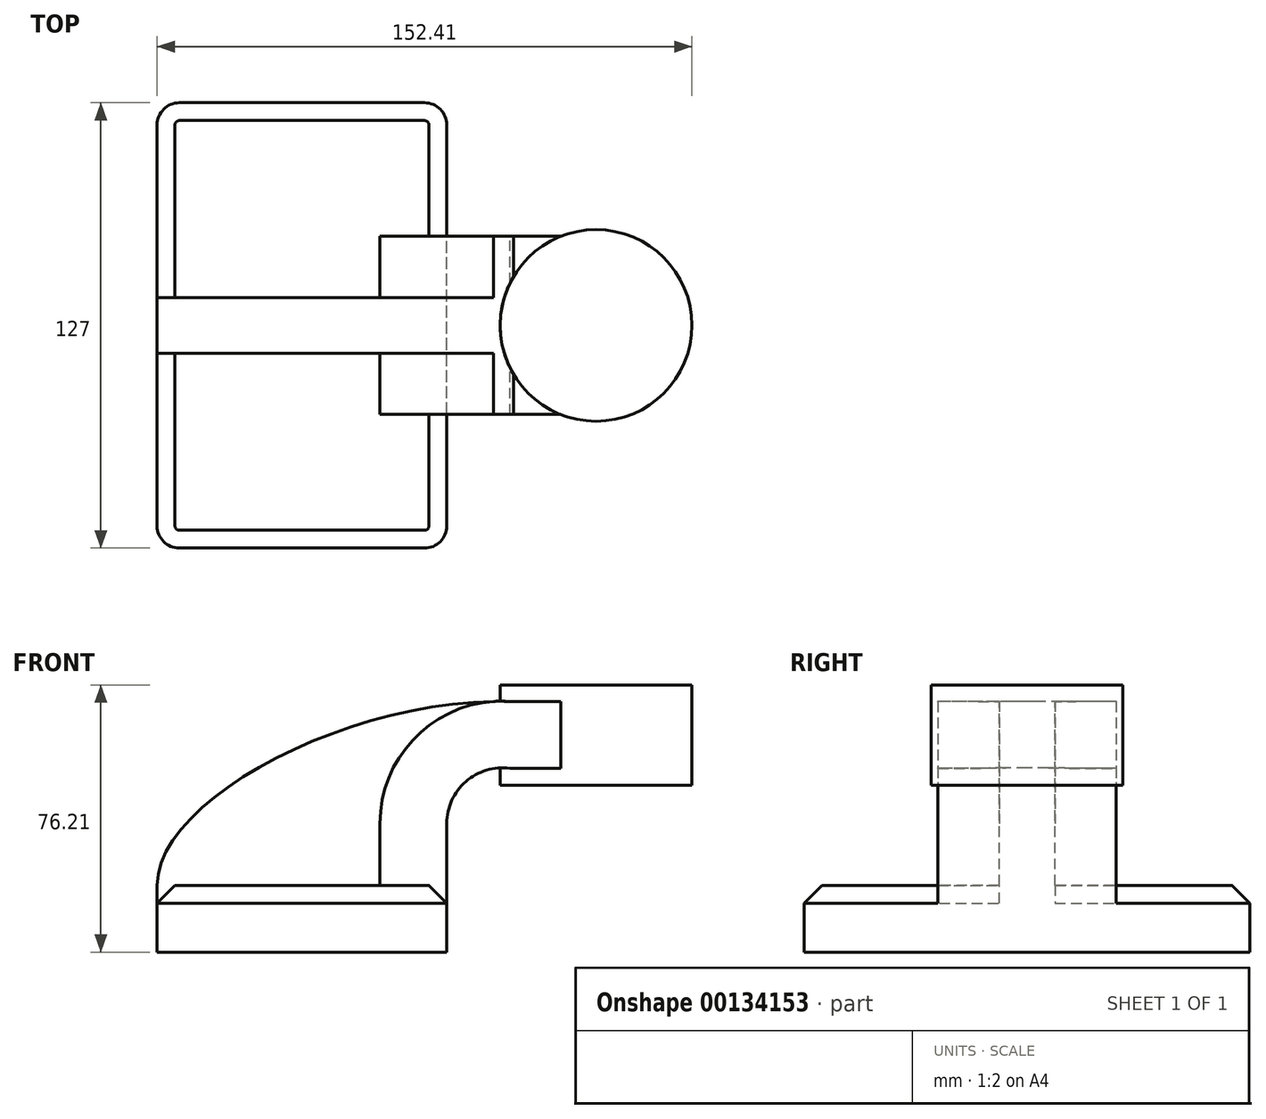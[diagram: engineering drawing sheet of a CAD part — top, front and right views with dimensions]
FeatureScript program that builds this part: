
annotation { "Feature Type Name" : "Feature", "Feature Type Description" : "" }
export const myFeature = defineFeature(function(context is Context, id is Id, definition is map)
    precondition{}
    {
        {
            var Q0;
            Q0=qCreatedBy(makeId("Front.planeOp"),FACE);
            var sketch = newSketch(context, id + "F0", { "sketchPlane" : qUnion([Q0])});
            skLineSegment(sketch, "E0.bottom", {"start": v(41.27, 9.53) * mm, "end": v(-41.28, 9.53) * mm});
            skLineSegment(sketch, "E0.top", {"start": v(41.28, -9.52) * mm, "end": v(-41.28, -9.52) * mm});
            skLineSegment(sketch, "E0.left", {"start": v(41.28, 9.53) * mm, "end": v(41.28, -9.52) * mm});
            skLineSegment(sketch, "E0.right", {"start": v(-41.28, 9.53) * mm, "end": v(-41.27, -9.52) * mm});
            skPoint(sketch, "E0.middle", {"position": v(0, 0) * mm});
            skLineSegment(sketch, "E1.bottom", {"start": v(111.12, 66.68) * mm, "end": v(60.32, 66.68) * mm});
            skLineSegment(sketch, "E1.top", {"start": v(111.12, 38.1) * mm, "end": v(60.32, 38.1) * mm});
            skLineSegment(sketch, "E1.left", {"start": v(111.12, 66.68) * mm, "end": v(111.12, 38.1) * mm});
            skLineSegment(sketch, "E1.right", {"start": v(60.32, 66.68) * mm, "end": v(60.32, 38.1) * mm});
            skPoint(sketch, "E1.middle", {"position": v(85.72, 52.39) * mm});
            skLineSegment(sketch, "E2", {"start": v(41.27, 9.53) * mm, "end": v(41.27, 27.14) * mm});
            skArc(sketch, "E3", {"start": v(41.27, 27.14) * mm, "mid": v(46.7, 39.09) * mm, "end": v(59.26, 42.88) * mm});
            skLineSegment(sketch, "E4", {"start": v(59.26, 42.88) * mm, "end": v(83.8, 42.88) * mm});
            skLineSegment(sketch, "E5.0", {"start": v(60.28, 61.93) * mm, "end": v(83.8, 61.93) * mm});
            skArc(sketch, "E5.1", {"start": v(22.22, 27.14) * mm, "mid": v(33.59, 52.92) * mm, "end": v(60.28, 61.93) * mm});
            skLineSegment(sketch, "E5.2", {"start": v(22.22, 9.53) * mm, "end": v(22.22, 27.14) * mm});
            skLineSegment(sketch, "E6", {"start": v(83.8, 38.1) * mm, "end": v(83.8, 66.68) * mm});
            skFitSpline(sketch, "E7", {"points": [v(-41.28, 9.53) * mm, v(60.28, 61.93) * mm], "startDerivative": vector(0.42, 75.47) * mm, "endDerivative": vector(135.73, -4.88) * mm});
            skSolve(sketch);
        }
        {
            var Q0;
            Q0=makeQuery(id+"F0.imprint","IMPRINT",FACE,{"disambiguationData":[TD([[makeQuery(id+"F0.imprint","IMPRINT",EDGE,{"derivedFrom":sQuery(id+"F0.wireOp",EDGE,"E0.top")}),-1.0]])]});
            extrude(context, id + "F1", {"entities" : qUnion([Q0]), "endBound" : BoundingType.SYMMETRIC, "depth" : 127 * mm});
        }
        {
            var Q0;
            {var subQ1=sQuery(id+"F0.wireOp",EDGE,"E2");Q0=makeQuery(id+"F0.imprint","IMPRINT",FACE,{"disambiguationData":[TD([[makeQuery(id+"F0.imprint","IMPRINT",EDGE,{"derivedFrom":subQ1}),1.0]])]});}
            var Q1;
            {var subQ0=sQuery(id+"F0.wireOp",EDGE,"E5.0");var subQ1=sQuery(id+"F0.wireOp",EDGE,"E1.right");var subQ2=makeQuery(id+"F0.imprint","INTERSECT",VERTEX,{"derivedFrom":[subQ1,subQ0]});Q1=makeQuery(id+"F0.imprint","IMPRINT",FACE,{"disambiguationData":[TD([[makeQuery(id+"F0.imprint","IMPRINT",EDGE,{"disambiguationData":[TD([[subQ2,-1.0]])],"derivedFrom":subQ1}),1.0]])]});}
            extrude(context, id + "F2", {"entities" : qUnion([Q0, Q1]), "operationType" : NewBodyOperationType.ADD, "endBound" : BoundingType.SYMMETRIC, "depth" : 50.8 * mm});
        }
        {
            var Q0;
            {var subQ3=sQuery(id+"F0.wireOp",EDGE,"E5.2");Q0=makeQuery(id+"F0.imprint","IMPRINT",FACE,{"disambiguationData":[TD([[makeQuery(id+"F0.imprint","IMPRINT",EDGE,{"derivedFrom":subQ3}),1.0]])]});}
            extrude(context, id + "F3", {"entities" : qUnion([Q0]), "operationType" : NewBodyOperationType.ADD, "endBound" : BoundingType.SYMMETRIC, "depth" : 15.88 * mm});
        }
        {
            var Q0;
            {var subQ0=sQuery(id+"F0.wireOp",EDGE,"E1.left");Q0=makeQuery(id+"F0.imprint","IMPRINT",FACE,{"disambiguationData":[TD([[makeQuery(id+"F0.imprint","IMPRINT",EDGE,{"derivedFrom":subQ0}),-1.0]])]});}
            var Q1;
            Q1=sQuery(id+"F0.wireOp",EDGE,"E6");
            revolve(context, id + "F4", {"operationType" : NewBodyOperationType.ADD, "entities" : qUnion([Q0]), "axis" : qUnion([Q1]), "revolveType" : RevolveType.FULL});
        }
        {
            var Q0;
            Q0=makeQuery(id+"F1.opExtrude","CAP_EDGE",EDGE,{"disambiguationData":[OSD([sQuery(id+"F0.wireOp",EDGE,"E0.right")])],"isStart":false});
            var Q1;
            Q1=makeQuery(id+"F1.opExtrude","CAP_EDGE",EDGE,{"disambiguationData":[OSD([sQuery(id+"F0.wireOp",EDGE,"E0.left")])],"isStart":false});
            var Q2;
            Q2=makeQuery(id+"F1.opExtrude","CAP_EDGE",EDGE,{"disambiguationData":[OSD([sQuery(id+"F0.wireOp",EDGE,"E0.left")])],"isStart":true});
            var Q3;
            Q3=makeQuery(id+"F1.opExtrude","CAP_EDGE",EDGE,{"disambiguationData":[OSD([sQuery(id+"F0.wireOp",EDGE,"E0.right")])],"isStart":true});
            fillet(context, id + "F5", {"entities" : qUnion([Q0, Q1, Q2, Q3]), "radius" : 6.35 * mm, "tangentPropagation" : true, "allowEdgeOverflow" : false});
        }
        {
            var Q0;
            Q0=makeQuery(id+"F1.opExtrude","CAP_EDGE",EDGE,{"disambiguationData":[OSD([sQuery(id+"F0.wireOp",EDGE,"E0.bottom")])],"isStart":false});
            var Q1;
            Q1=makeQuery(id+"F1.opExtrude","CAP_EDGE",EDGE,{"disambiguationData":[OSD([sQuery(id+"F0.wireOp",EDGE,"E0.bottom")])],"isStart":true});
            chamfer(context, id + "F6", {"entities" : qUnion([Q0, Q1]), "width" : 5.08 * mm, "tangentPropagation" : true});
        }
    });
